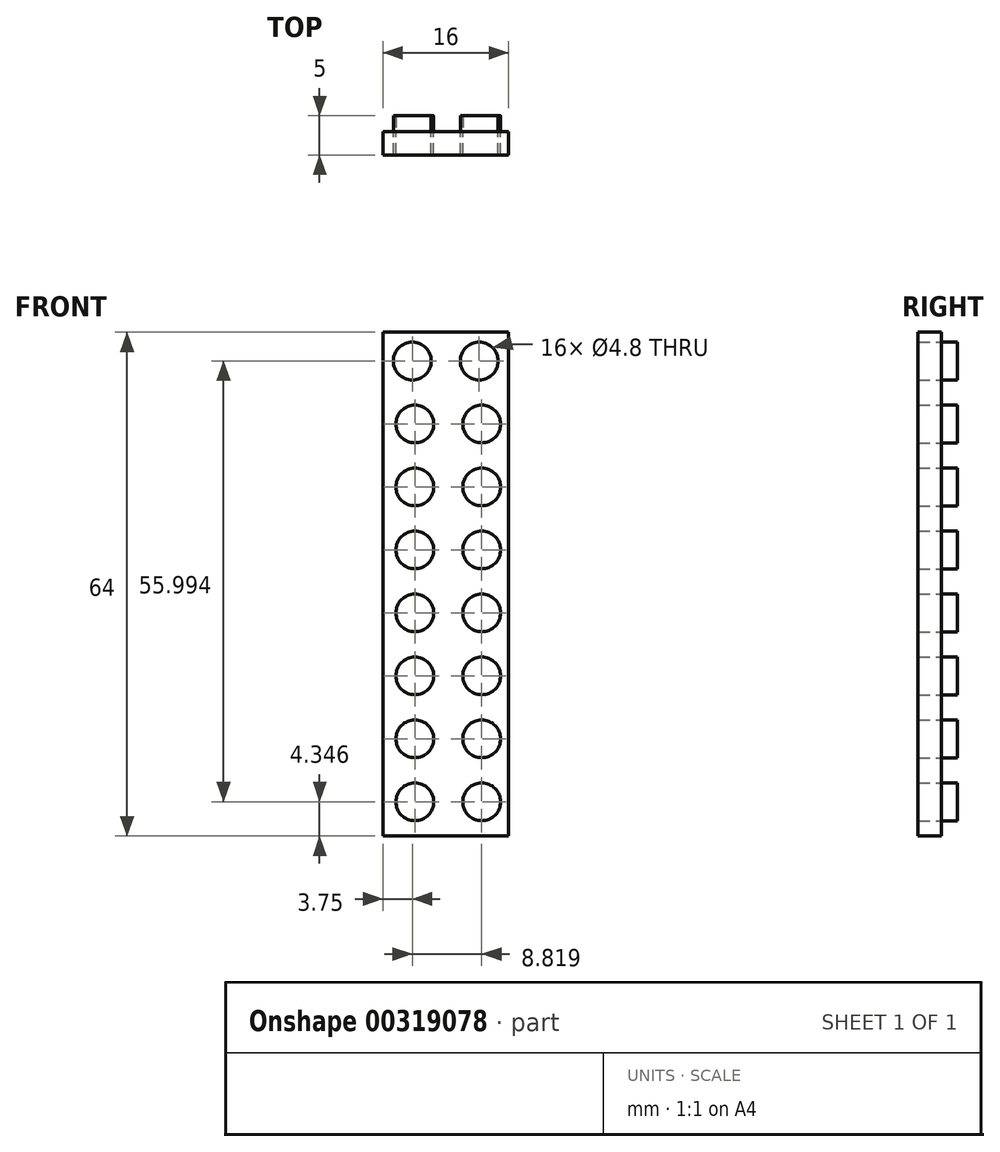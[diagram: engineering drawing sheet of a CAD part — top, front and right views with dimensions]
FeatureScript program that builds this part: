
annotation { "Feature Type Name" : "Feature", "Feature Type Description" : "" }
export const myFeature = defineFeature(function(context is Context, id is Id, definition is map)
    precondition{}
    {
        {
            var Q0;
            Q0=qCreatedBy(makeId("Front.planeOp"),FACE);
            var sketch = newSketch(context, id + "F0", { "sketchPlane" : qUnion([Q0])});
            skLineSegment(sketch, "E0.bottom", {"start": v(-8, -32) * mm, "end": v(8, -32) * mm});
            skLineSegment(sketch, "E0.top", {"start": v(-8, 32) * mm, "end": v(8, 32) * mm});
            skLineSegment(sketch, "E0.left", {"start": v(-8, -32) * mm, "end": v(-8, 32) * mm});
            skLineSegment(sketch, "E0.right", {"start": v(8, -32) * mm, "end": v(8, 32) * mm});
            skPoint(sketch, "E0.middle", {"position": v(0, 0) * mm});
            skCircle(sketch, "E1", {"center": v(-4.25, 28.34) * mm, "radius": 2.4 * mm});
            skCircle(sketch, "E2", {"center": v(4.25, 28.34) * mm, "radius": 2.4 * mm});
            skCircle(sketch, "E3", {"center": v(-3.93, 20.35) * mm, "radius": 2.4 * mm});
            skCircle(sketch, "E4", {"center": v(-3.93, 12.35) * mm, "radius": 2.4 * mm});
            skCircle(sketch, "E5", {"center": v(-3.93, 4.35) * mm, "radius": 2.4 * mm});
            skCircle(sketch, "E6", {"center": v(-3.93, -3.65) * mm, "radius": 2.4 * mm});
            skCircle(sketch, "E7", {"center": v(-3.93, -11.65) * mm, "radius": 2.4 * mm});
            skCircle(sketch, "E8", {"center": v(-3.93, -19.65) * mm, "radius": 2.4 * mm});
            skCircle(sketch, "E9", {"center": v(-3.93, -27.65) * mm, "radius": 2.4 * mm});
            skCircle(sketch, "E10", {"center": v(4.57, 20.35) * mm, "radius": 2.4 * mm});
            skCircle(sketch, "E11", {"center": v(4.57, 12.35) * mm, "radius": 2.4 * mm});
            skCircle(sketch, "E12", {"center": v(4.57, 4.35) * mm, "radius": 2.4 * mm});
            skCircle(sketch, "E13", {"center": v(4.57, -3.65) * mm, "radius": 2.4 * mm});
            skCircle(sketch, "E14", {"center": v(4.57, -11.65) * mm, "radius": 2.4 * mm});
            skCircle(sketch, "E15", {"center": v(4.57, -19.65) * mm, "radius": 2.4 * mm});
            skCircle(sketch, "E16", {"center": v(4.57, -27.65) * mm, "radius": 2.4 * mm});
            skSolve(sketch);
        }
        {
            var Q0;
            Q0=makeQuery(id+"F0.imprint","IMPRINT",FACE,{"disambiguationData":[TD([[makeQuery(id+"F0.imprint","IMPRINT",EDGE,{"derivedFrom":sQuery(id+"F0.wireOp",EDGE,"E0.bottom")}),1.0]])]});
            extrude(context, id + "F1", {"entities" : qUnion([Q0]), "depth" : 3 * mm});
        }
        {
            var Q0;
            Q0=makeQuery(id+"F0.imprint","IMPRINT",FACE,{"disambiguationData":[TD([[makeQuery(id+"F0.imprint","IMPRINT",EDGE,{"derivedFrom":sQuery(id+"F0.wireOp",EDGE,"E1")}),1.0]])]});
            var Q1;
            Q1=makeQuery(id+"F0.imprint","IMPRINT",FACE,{"disambiguationData":[TD([[makeQuery(id+"F0.imprint","IMPRINT",EDGE,{"derivedFrom":sQuery(id+"F0.wireOp",EDGE,"E3")}),1.0]])]});
            var Q2;
            Q2=makeQuery(id+"F0.imprint","IMPRINT",FACE,{"disambiguationData":[TD([[makeQuery(id+"F0.imprint","IMPRINT",EDGE,{"derivedFrom":sQuery(id+"F0.wireOp",EDGE,"E4")}),1.0]])]});
            var Q3;
            Q3=makeQuery(id+"F0.imprint","IMPRINT",FACE,{"disambiguationData":[TD([[makeQuery(id+"F0.imprint","IMPRINT",EDGE,{"derivedFrom":sQuery(id+"F0.wireOp",EDGE,"E5")}),1.0]])]});
            var Q4;
            Q4=makeQuery(id+"F0.imprint","IMPRINT",FACE,{"disambiguationData":[TD([[makeQuery(id+"F0.imprint","IMPRINT",EDGE,{"derivedFrom":sQuery(id+"F0.wireOp",EDGE,"E6")}),1.0]])]});
            var Q5;
            Q5=makeQuery(id+"F0.imprint","IMPRINT",FACE,{"disambiguationData":[TD([[makeQuery(id+"F0.imprint","IMPRINT",EDGE,{"derivedFrom":sQuery(id+"F0.wireOp",EDGE,"E7")}),1.0]])]});
            var Q6;
            Q6=makeQuery(id+"F0.imprint","IMPRINT",FACE,{"disambiguationData":[TD([[makeQuery(id+"F0.imprint","IMPRINT",EDGE,{"derivedFrom":sQuery(id+"F0.wireOp",EDGE,"E8")}),1.0]])]});
            var Q7;
            Q7=makeQuery(id+"F0.imprint","IMPRINT",FACE,{"disambiguationData":[TD([[makeQuery(id+"F0.imprint","IMPRINT",EDGE,{"derivedFrom":sQuery(id+"F0.wireOp",EDGE,"E9")}),1.0]])]});
            var Q8;
            Q8=makeQuery(id+"F0.imprint","IMPRINT",FACE,{"disambiguationData":[TD([[makeQuery(id+"F0.imprint","IMPRINT",EDGE,{"derivedFrom":sQuery(id+"F0.wireOp",EDGE,"E2")}),1.0]])]});
            var Q9;
            Q9=makeQuery(id+"F0.imprint","IMPRINT",FACE,{"disambiguationData":[TD([[makeQuery(id+"F0.imprint","IMPRINT",EDGE,{"derivedFrom":sQuery(id+"F0.wireOp",EDGE,"E10")}),1.0]])]});
            var Q10;
            Q10=makeQuery(id+"F0.imprint","IMPRINT",FACE,{"disambiguationData":[TD([[makeQuery(id+"F0.imprint","IMPRINT",EDGE,{"derivedFrom":sQuery(id+"F0.wireOp",EDGE,"E12")}),1.0]])]});
            var Q11;
            Q11=makeQuery(id+"F0.imprint","IMPRINT",FACE,{"disambiguationData":[TD([[makeQuery(id+"F0.imprint","IMPRINT",EDGE,{"derivedFrom":sQuery(id+"F0.wireOp",EDGE,"E11")}),1.0]])]});
            var Q12;
            Q12=makeQuery(id+"F0.imprint","IMPRINT",FACE,{"disambiguationData":[TD([[makeQuery(id+"F0.imprint","IMPRINT",EDGE,{"derivedFrom":sQuery(id+"F0.wireOp",EDGE,"E13")}),1.0]])]});
            var Q13;
            Q13=makeQuery(id+"F0.imprint","IMPRINT",FACE,{"disambiguationData":[TD([[makeQuery(id+"F0.imprint","IMPRINT",EDGE,{"derivedFrom":sQuery(id+"F0.wireOp",EDGE,"E14")}),1.0]])]});
            var Q14;
            Q14=makeQuery(id+"F0.imprint","IMPRINT",FACE,{"disambiguationData":[TD([[makeQuery(id+"F0.imprint","IMPRINT",EDGE,{"derivedFrom":sQuery(id+"F0.wireOp",EDGE,"E15")}),1.0]])]});
            var Q15;
            Q15=makeQuery(id+"F0.imprint","IMPRINT",FACE,{"disambiguationData":[TD([[makeQuery(id+"F0.imprint","IMPRINT",EDGE,{"derivedFrom":sQuery(id+"F0.wireOp",EDGE,"E16")}),1.0]])]});
            extrude(context, id + "F2", {"entities" : qUnion([Q0, Q1, Q2, Q3, Q4, Q5, Q6, Q7, Q8, Q9, Q10, Q11, Q12, Q13, Q14, Q15]), "operationType" : NewBodyOperationType.ADD, "oppositeDirection" : true, "depth" : 2 * mm});
        }
    });
